# Revit family: ASL_Designline_Timber_Door_Head
name_source: partatom
category: Detail Items
revit_build: Autodesk Revit 2018 (Build: 20170223_1515(x64)
units: mm (PartAtom-declared; Revit-internal decimal feet)

## family parameters
Rotate with component = No
Section Shape = Not Defined
Shared = Yes

## types (3) — shared parameters
Head = Yes
Manufacturer = Aluminate Solutions Limited
Technical Info = www.aluminate.nz

## per-type parameters (varying)
| type | 40mm Door Jamb Standard | 50mm Door Jamb Standard | Door_40 | Door_50 | Glazing | Masking Region Parametric_1 | Masking Region Parametric_2 | Type Comments |
| Glazing | No | No | No | No | Yes | 23 mm | 22 mm  [stored 0.0721785 ft] | ASL Designline Head With Single Action 50mm Timber Door |
| Single Action Door 40mm | Yes | No | Yes | No | No | 23 mm | 27 mm  [stored 0.0885827 ft] | ASL Designline Head With Single Action 40mm Timber Door |
| Single Action Door 50mm | No | Yes | No | Yes | No | 25 mm  [stored 0.082021 ft] | 32 mm | ASL Designline Head With Single Action 50mm Timber Door |

note: [stored X ft] marks values corroborated as IEEE doubles in the binary element streams (Revit-internal decimal feet)

## geometry (parser evidence)
native form markers: Sweep x8
no freeform markers — native parametric forms only
